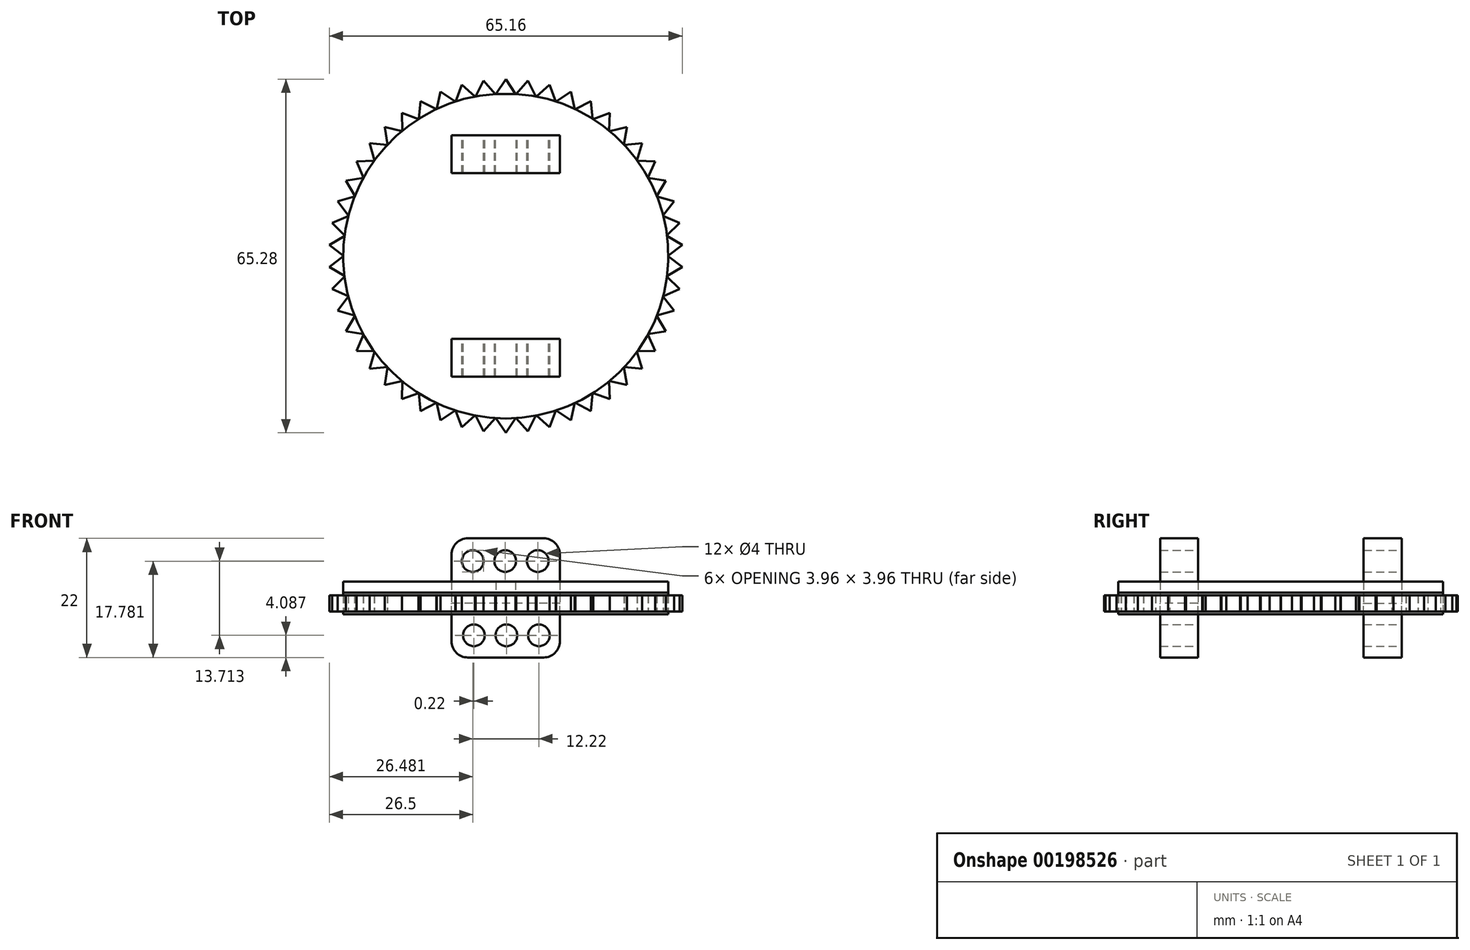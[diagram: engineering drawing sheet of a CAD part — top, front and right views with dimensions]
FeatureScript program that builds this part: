
annotation { "Feature Type Name" : "Feature", "Feature Type Description" : "" }
export const myFeature = defineFeature(function(context is Context, id is Id, definition is map)
    precondition{}
    {
        {
            var Q0;
            Q0=qCreatedBy(makeId("Top.planeOp"),FACE);
            var sketch = newSketch(context, id + "F0", { "sketchPlane" : qUnion([Q0])});
            skCircle(sketch, "E0", {"center": v(0, 0) * mm, "radius": 30 * mm});
            skLineSegment(sketch, "E1", {"start": v(0, 35.87) * mm, "end": v(0, -34.78) * mm, "construction": true});
            skLineSegment(sketch, "E2", {"start": v(-1.83, 29.94) * mm, "end": v(0, 32.64) * mm});
            skLineSegment(sketch, "E3.MirrorCS", {"start": v(1.83, 29.94) * mm, "end": v(0, 32.64) * mm});
            skLineSegment(sketch, "E4", {"start": v(-1.83, 29.94) * mm, "end": v(1.83, 29.94) * mm});
            skLineSegment(sketch, "E5.1.0", {"start": v(-5.57, 29.48) * mm, "end": v(-4.1, 32.39) * mm});
            skLineSegment(sketch, "E5.1.1", {"start": v(-1.94, 29.94) * mm, "end": v(-4.1, 32.39) * mm});
            skLineSegment(sketch, "E5.2.0", {"start": v(-9.22, 28.55) * mm, "end": v(-8.12, 31.62) * mm});
            skLineSegment(sketch, "E5.2.1", {"start": v(-5.68, 29.46) * mm, "end": v(-8.12, 31.62) * mm});
            skLineSegment(sketch, "E5.3.0", {"start": v(-12.72, 27.17) * mm, "end": v(-12.02, 30.35) * mm});
            skLineSegment(sketch, "E5.3.1", {"start": v(-9.33, 28.51) * mm, "end": v(-12.02, 30.35) * mm});
            skLineSegment(sketch, "E5.4.0", {"start": v(-16.03, 25.36) * mm, "end": v(-15.73, 28.6) * mm});
            skLineSegment(sketch, "E5.4.1", {"start": v(-12.83, 27.12) * mm, "end": v(-15.73, 28.6) * mm});
            skLineSegment(sketch, "E5.5.0", {"start": v(-19.08, 23.15) * mm, "end": v(-19.19, 26.4) * mm});
            skLineSegment(sketch, "E5.5.1", {"start": v(-16.12, 25.3) * mm, "end": v(-19.19, 26.4) * mm});
            skLineSegment(sketch, "E5.6.0", {"start": v(-21.83, 20.58) * mm, "end": v(-22.35, 23.8) * mm});
            skLineSegment(sketch, "E5.6.1", {"start": v(-19.17, 23.08) * mm, "end": v(-22.35, 23.8) * mm});
            skLineSegment(sketch, "E5.7.0", {"start": v(-24.24, 17.68) * mm, "end": v(-25.15, 20.8) * mm});
            skLineSegment(sketch, "E5.7.1", {"start": v(-21.9, 20.5) * mm, "end": v(-25.15, 20.8) * mm});
            skLineSegment(sketch, "E5.8.0", {"start": v(-26.26, 14.5) * mm, "end": v(-27.56, 17.5) * mm});
            skLineSegment(sketch, "E5.8.1", {"start": v(-24.3, 17.59) * mm, "end": v(-27.56, 17.5) * mm});
            skLineSegment(sketch, "E5.9.0", {"start": v(-27.87, 11.1) * mm, "end": v(-29.54, 13.9) * mm});
            skLineSegment(sketch, "E5.9.1", {"start": v(-26.32, 14.4) * mm, "end": v(-29.54, 13.9) * mm});
            skLineSegment(sketch, "E5.10.0", {"start": v(-29.04, 7.52) * mm, "end": v(-31.05, 10.09) * mm});
            skLineSegment(sketch, "E5.10.1", {"start": v(-27.91, 11) * mm, "end": v(-31.05, 10.09) * mm});
            skLineSegment(sketch, "E5.11.0", {"start": v(-29.76, 3.82) * mm, "end": v(-32.07, 6.12) * mm});
            skLineSegment(sketch, "E5.11.1", {"start": v(-29.07, 7.4) * mm, "end": v(-32.07, 6.12) * mm});
            skLineSegment(sketch, "E5.12.0", {"start": v(-30, 0.06) * mm, "end": v(-32.58, 2.05) * mm});
            skLineSegment(sketch, "E5.12.1", {"start": v(-29.77, 3.7) * mm, "end": v(-32.58, 2.05) * mm});
            skLineSegment(sketch, "E5.13.0", {"start": v(-29.77, -3.7) * mm, "end": v(-32.58, -2.05) * mm});
            skLineSegment(sketch, "E5.13.1", {"start": v(-30, -0.06) * mm, "end": v(-32.58, -2.05) * mm});
            skLineSegment(sketch, "E5.14.0", {"start": v(-29.07, -7.4) * mm, "end": v(-32.07, -6.12) * mm});
            skLineSegment(sketch, "E5.14.1", {"start": v(-29.76, -3.82) * mm, "end": v(-32.07, -6.12) * mm});
            skLineSegment(sketch, "E5.15.0", {"start": v(-27.91, -11) * mm, "end": v(-31.05, -10.09) * mm});
            skLineSegment(sketch, "E5.15.1", {"start": v(-29.04, -7.52) * mm, "end": v(-31.05, -10.09) * mm});
            skLineSegment(sketch, "E5.16.0", {"start": v(-26.32, -14.4) * mm, "end": v(-29.54, -13.9) * mm});
            skLineSegment(sketch, "E5.16.1", {"start": v(-27.87, -11.1) * mm, "end": v(-29.54, -13.9) * mm});
            skLineSegment(sketch, "E5.17.0", {"start": v(-24.3, -17.59) * mm, "end": v(-27.56, -17.5) * mm});
            skLineSegment(sketch, "E5.17.1", {"start": v(-26.26, -14.5) * mm, "end": v(-27.56, -17.5) * mm});
            skLineSegment(sketch, "E5.18.0", {"start": v(-21.9, -20.5) * mm, "end": v(-25.15, -20.8) * mm});
            skLineSegment(sketch, "E5.18.1", {"start": v(-24.24, -17.68) * mm, "end": v(-25.15, -20.8) * mm});
            skLineSegment(sketch, "E5.19.0", {"start": v(-19.17, -23.08) * mm, "end": v(-22.35, -23.8) * mm});
            skLineSegment(sketch, "E5.19.1", {"start": v(-21.83, -20.58) * mm, "end": v(-22.35, -23.8) * mm});
            skLineSegment(sketch, "E5.20.0", {"start": v(-16.12, -25.3) * mm, "end": v(-19.19, -26.4) * mm});
            skLineSegment(sketch, "E5.20.1", {"start": v(-19.08, -23.15) * mm, "end": v(-19.19, -26.4) * mm});
            skLineSegment(sketch, "E5.21.0", {"start": v(-12.83, -27.12) * mm, "end": v(-15.73, -28.6) * mm});
            skLineSegment(sketch, "E5.21.1", {"start": v(-16.03, -25.36) * mm, "end": v(-15.73, -28.6) * mm});
            skLineSegment(sketch, "E5.22.0", {"start": v(-9.33, -28.51) * mm, "end": v(-12.02, -30.35) * mm});
            skLineSegment(sketch, "E5.22.1", {"start": v(-12.72, -27.17) * mm, "end": v(-12.02, -30.35) * mm});
            skLineSegment(sketch, "E5.23.0", {"start": v(-5.68, -29.46) * mm, "end": v(-8.12, -31.62) * mm});
            skLineSegment(sketch, "E5.23.1", {"start": v(-9.22, -28.55) * mm, "end": v(-8.12, -31.62) * mm});
            skLineSegment(sketch, "E5.24.0", {"start": v(-1.94, -29.94) * mm, "end": v(-4.1, -32.39) * mm});
            skLineSegment(sketch, "E5.24.1", {"start": v(-5.57, -29.48) * mm, "end": v(-4.1, -32.39) * mm});
            skLineSegment(sketch, "E5.25.0", {"start": v(1.83, -29.94) * mm, "end": v(0, -32.64) * mm});
            skLineSegment(sketch, "E5.25.1", {"start": v(-1.83, -29.94) * mm, "end": v(0, -32.64) * mm});
            skLineSegment(sketch, "E5.26.0", {"start": v(5.57, -29.48) * mm, "end": v(4.1, -32.39) * mm});
            skLineSegment(sketch, "E5.26.1", {"start": v(1.94, -29.94) * mm, "end": v(4.1, -32.39) * mm});
            skLineSegment(sketch, "E5.27.0", {"start": v(9.22, -28.55) * mm, "end": v(8.12, -31.62) * mm});
            skLineSegment(sketch, "E5.27.1", {"start": v(5.68, -29.46) * mm, "end": v(8.12, -31.62) * mm});
            skLineSegment(sketch, "E5.28.0", {"start": v(12.72, -27.17) * mm, "end": v(12.02, -30.35) * mm});
            skLineSegment(sketch, "E5.28.1", {"start": v(9.33, -28.51) * mm, "end": v(12.02, -30.35) * mm});
            skLineSegment(sketch, "E5.29.0", {"start": v(16.03, -25.36) * mm, "end": v(15.73, -28.6) * mm});
            skLineSegment(sketch, "E5.29.1", {"start": v(12.83, -27.12) * mm, "end": v(15.73, -28.6) * mm});
            skLineSegment(sketch, "E5.30.0", {"start": v(19.08, -23.15) * mm, "end": v(19.19, -26.4) * mm});
            skLineSegment(sketch, "E5.30.1", {"start": v(16.12, -25.3) * mm, "end": v(19.19, -26.4) * mm});
            skLineSegment(sketch, "E5.31.0", {"start": v(21.83, -20.58) * mm, "end": v(22.35, -23.8) * mm});
            skLineSegment(sketch, "E5.31.1", {"start": v(19.17, -23.08) * mm, "end": v(22.35, -23.8) * mm});
            skLineSegment(sketch, "E5.32.0", {"start": v(24.24, -17.68) * mm, "end": v(25.15, -20.8) * mm});
            skLineSegment(sketch, "E5.32.1", {"start": v(21.9, -20.5) * mm, "end": v(25.15, -20.8) * mm});
            skLineSegment(sketch, "E5.33.0", {"start": v(26.26, -14.5) * mm, "end": v(27.56, -17.5) * mm});
            skLineSegment(sketch, "E5.33.1", {"start": v(24.3, -17.59) * mm, "end": v(27.56, -17.5) * mm});
            skLineSegment(sketch, "E5.34.0", {"start": v(27.87, -11.1) * mm, "end": v(29.54, -13.9) * mm});
            skLineSegment(sketch, "E5.34.1", {"start": v(26.32, -14.4) * mm, "end": v(29.54, -13.9) * mm});
            skLineSegment(sketch, "E5.35.0", {"start": v(29.04, -7.52) * mm, "end": v(31.05, -10.09) * mm});
            skLineSegment(sketch, "E5.35.1", {"start": v(27.91, -11) * mm, "end": v(31.05, -10.09) * mm});
            skLineSegment(sketch, "E5.36.0", {"start": v(29.76, -3.82) * mm, "end": v(32.07, -6.12) * mm});
            skLineSegment(sketch, "E5.36.1", {"start": v(29.07, -7.4) * mm, "end": v(32.07, -6.12) * mm});
            skLineSegment(sketch, "E5.37.0", {"start": v(30, -0.06) * mm, "end": v(32.58, -2.05) * mm});
            skLineSegment(sketch, "E5.37.1", {"start": v(29.77, -3.7) * mm, "end": v(32.58, -2.05) * mm});
            skLineSegment(sketch, "E5.38.0", {"start": v(29.77, 3.7) * mm, "end": v(32.58, 2.05) * mm});
            skLineSegment(sketch, "E5.38.1", {"start": v(30, 0.06) * mm, "end": v(32.58, 2.05) * mm});
            skLineSegment(sketch, "E5.39.0", {"start": v(29.07, 7.4) * mm, "end": v(32.07, 6.12) * mm});
            skLineSegment(sketch, "E5.39.1", {"start": v(29.76, 3.82) * mm, "end": v(32.07, 6.12) * mm});
            skLineSegment(sketch, "E5.40.0", {"start": v(27.91, 11) * mm, "end": v(31.05, 10.09) * mm});
            skLineSegment(sketch, "E5.40.1", {"start": v(29.04, 7.52) * mm, "end": v(31.05, 10.09) * mm});
            skLineSegment(sketch, "E5.41.0", {"start": v(26.32, 14.4) * mm, "end": v(29.54, 13.9) * mm});
            skLineSegment(sketch, "E5.41.1", {"start": v(27.87, 11.1) * mm, "end": v(29.54, 13.9) * mm});
            skLineSegment(sketch, "E5.42.0", {"start": v(24.3, 17.59) * mm, "end": v(27.56, 17.5) * mm});
            skLineSegment(sketch, "E5.42.1", {"start": v(26.26, 14.5) * mm, "end": v(27.56, 17.5) * mm});
            skLineSegment(sketch, "E5.43.0", {"start": v(21.9, 20.5) * mm, "end": v(25.15, 20.8) * mm});
            skLineSegment(sketch, "E5.43.1", {"start": v(24.24, 17.68) * mm, "end": v(25.15, 20.8) * mm});
            skLineSegment(sketch, "E5.44.0", {"start": v(19.17, 23.08) * mm, "end": v(22.35, 23.8) * mm});
            skLineSegment(sketch, "E5.44.1", {"start": v(21.83, 20.58) * mm, "end": v(22.35, 23.8) * mm});
            skLineSegment(sketch, "E5.45.0", {"start": v(16.12, 25.3) * mm, "end": v(19.19, 26.4) * mm});
            skLineSegment(sketch, "E5.45.1", {"start": v(19.08, 23.15) * mm, "end": v(19.19, 26.4) * mm});
            skLineSegment(sketch, "E5.46.0", {"start": v(12.83, 27.12) * mm, "end": v(15.73, 28.6) * mm});
            skLineSegment(sketch, "E5.46.1", {"start": v(16.03, 25.36) * mm, "end": v(15.73, 28.6) * mm});
            skLineSegment(sketch, "E5.47.0", {"start": v(9.33, 28.51) * mm, "end": v(12.02, 30.35) * mm});
            skLineSegment(sketch, "E5.47.1", {"start": v(12.72, 27.17) * mm, "end": v(12.02, 30.35) * mm});
            skLineSegment(sketch, "E5.48.0", {"start": v(5.68, 29.46) * mm, "end": v(8.12, 31.62) * mm});
            skLineSegment(sketch, "E5.48.1", {"start": v(9.22, 28.55) * mm, "end": v(8.12, 31.62) * mm});
            skLineSegment(sketch, "E5.49.0", {"start": v(1.94, 29.94) * mm, "end": v(4.1, 32.39) * mm});
            skLineSegment(sketch, "E5.49.1", {"start": v(5.57, 29.48) * mm, "end": v(4.1, 32.39) * mm});
            skSolve(sketch);
        }
        {
            var Q0;
            Q0 = qSketchRegion(id + "F0", true);
            extrude(context, id + "F1", {"entities" : qUnion([Q0]), "endBound" : BoundingType.SYMMETRIC, "depth" : 3 * mm});
        }
        {
            var Q0;
            {var subQ56=sQuery(id+"F0.wireOp",EDGE,"E4");Q0=makeQuery(id+"F0.imprint","IMPRINT",FACE,{"disambiguationData":[TD([[makeQuery(id+"F0.imprint","IMPRINT",EDGE,{"derivedFrom":subQ56}),-1.0]])]});}
            extrude(context, id + "F2", {"entities" : qUnion([Q0]), "endBound" : BoundingType.SYMMETRIC, "depth" : 4 * mm});
        }
        {
            var Q0;
            Q0=makeQuery(id+"F2.opExtrude","CAP_FACE",FACE,{"disambiguationData":[OSD([sQuery(id+"F0.wireOp",EDGE,"E0"),sQuery(id+"F0.wireOp",EDGE,"E4")])],"isStart":false});
            var Q1;
            Q1=sQuery(id+"F0.wireOp",EDGE,"E0");
            extrude(context, id + "F3", {"entities" : qUnion([Q0]), "surfaceEntities" : qUnion([Q1]), "depth" : 2 * mm});
        }
        {
            var Q0;
            Q0=qCreatedBy(makeId("Top.planeOp"),FACE);
            var sketch = newSketch(context, id + "F4", { "sketchPlane" : qUnion([Q0])});
            skLineSegment(sketch, "E6.bottom", {"start": v(10, 15.28) * mm, "end": v(-10, 15.28) * mm});
            skLineSegment(sketch, "E6.top", {"start": v(10, 22.28) * mm, "end": v(-10, 22.28) * mm});
            skLineSegment(sketch, "E6.left", {"start": v(10, 15.28) * mm, "end": v(10, 22.28) * mm});
            skLineSegment(sketch, "E6.right", {"start": v(-10, 15.28) * mm, "end": v(-10, 22.28) * mm});
            skLineSegment(sketch, "E7", {"start": v(0, -38.44) * mm, "end": v(0, 57.13) * mm, "construction": true});
            skLineSegment(sketch, "E8", {"start": v(36.72, 0) * mm, "end": v(-39.04, 0) * mm, "construction": true});
            skSolve(sketch);
        }
        {
            var Q0;
            Q0 = qSketchRegion(id + "F4", true);
            extrude(context, id + "F5", {"entities" : qUnion([Q0]), "depth" : 12 * mm});
        }
        {
            var Q0;
            Q0=makeQuery(id+"F5.opExtrude","CAP_EDGE",EDGE,{"disambiguationData":[OSD([sQuery(id+"F4.wireOp",EDGE,"E6.left")])],"isStart":false});
            var Q1;
            Q1=makeQuery(id+"F5.opExtrude","CAP_EDGE",EDGE,{"disambiguationData":[OSD([sQuery(id+"F4.wireOp",EDGE,"E6.right")])],"isStart":false});
            fillet(context, id + "F6", {"entities" : qUnion([Q0, Q1]), "radius" : 3 * mm, "tangentPropagation" : true, "allowEdgeOverflow" : false});
        }
        {
            var Q0;
            Q0=makeQuery(id+"F5.opExtrude","SWEPT_BODY",BODY,{"disambiguationData":[OSD([sQuery(id+"F4.wireOp",EDGE,"E6.bottom"),sQuery(id+"F4.wireOp",EDGE,"E6.top"),sQuery(id+"F4.wireOp",EDGE,"E6.left"),sQuery(id+"F4.wireOp",EDGE,"E6.right")])]});
            var Q1;
            Q1=qCreatedBy(makeId("Front.planeOp"),FACE);
            mirror(context, id + "F7", {"entities" : qUnion([Q0]), "mirrorPlane" : qUnion([Q1])});
        }
        {
            var Q0;
            Q0=qCreatedBy(makeId("Front.planeOp"),FACE);
            var sketch = newSketch(context, id + "F8", { "sketchPlane" : qUnion([Q0])});
            skCircle(sketch, "E9", {"center": v(5.9, 7.8) * mm, "radius": 2 * mm});
            skCircle(sketch, "E10.1.0.0", {"center": v(-0.1, 7.8) * mm, "radius": 2 * mm});
            skCircle(sketch, "E10.2.0.0", {"center": v(-6.1, 7.8) * mm, "radius": 2 * mm});
            skLineSegment(sketch, "E10.direction1", {"start": v(5.9, 7.8) * mm, "end": v(-0.1, 7.8) * mm, "construction": true});
            skSolve(sketch);
        }
        {
            var Q0;
            Q0 = qSketchRegion(id + "F8", true);
            extrude(context, id + "F9", {"entities" : qUnion([Q0]), "operationType" : NewBodyOperationType.REMOVE, "endBound" : BoundingType.SYMMETRIC, "depth" : 50 * mm});
        }
        {
            var Q0;
            Q0 = qSketchRegion(id + "F4", true);
            extrude(context, id + "F10", {"entities" : qUnion([Q0]), "oppositeDirection" : true, "depth" : 10 * mm});
        }
        {
            var Q0;
            Q0=makeQuery(id+"F10.opExtrude","CAP_EDGE",EDGE,{"disambiguationData":[OSD([sQuery(id+"F4.wireOp",EDGE,"E6.left")])],"isStart":false});
            var Q1;
            Q1=makeQuery(id+"F10.opExtrude","CAP_EDGE",EDGE,{"disambiguationData":[OSD([sQuery(id+"F4.wireOp",EDGE,"E6.right")])],"isStart":false});
            fillet(context, id + "F11", {"entities" : qUnion([Q0, Q1]), "radius" : 3 * mm, "tangentPropagation" : true, "allowEdgeOverflow" : false});
        }
        {
            var Q0;
            Q0=makeQuery(id+"F10.opExtrude","SWEPT_BODY",BODY,{"disambiguationData":[OSD([sQuery(id+"F4.wireOp",EDGE,"E6.bottom"),sQuery(id+"F4.wireOp",EDGE,"E6.top"),sQuery(id+"F4.wireOp",EDGE,"E6.left"),sQuery(id+"F4.wireOp",EDGE,"E6.right")])]});
            var Q1;
            Q1=qCreatedBy(makeId("Front.planeOp"),FACE);
            mirror(context, id + "F12", {"entities" : qUnion([Q0]), "mirrorPlane" : qUnion([Q1])});
        }
        {
            var Q0;
            Q0=qCreatedBy(makeId("Front.planeOp"),FACE);
            var sketch = newSketch(context, id + "F13", { "sketchPlane" : qUnion([Q0])});
            skCircle(sketch, "E11", {"center": v(6.12, -5.91) * mm, "radius": 2 * mm});
            skCircle(sketch, "E12.1.0.0", {"center": v(0.12, -5.91) * mm, "radius": 2 * mm});
            skCircle(sketch, "E12.2.0.0", {"center": v(-5.88, -5.91) * mm, "radius": 2 * mm});
            skLineSegment(sketch, "E12.direction1", {"start": v(6.12, -5.91) * mm, "end": v(0.12, -5.91) * mm, "construction": true});
            skSolve(sketch);
        }
        {
            var Q0;
            Q0 = qSketchRegion(id + "F13", true);
            var Q1;
            Q1=sQuery(id+"F13.wireOp",EDGE,"E11");
            var Q2;
            Q2=sQuery(id+"F13.wireOp",EDGE,"E12.1.0.0");
            var Q3;
            Q3=sQuery(id+"F13.wireOp",EDGE,"E12.2.0.0");
            extrude(context, id + "F14", {"entities" : qUnion([Q0]), "operationType" : NewBodyOperationType.REMOVE, "surfaceEntities" : qUnion([Q1, Q2, Q3]), "endBound" : BoundingType.SYMMETRIC, "depth" : 50 * mm});
        }
    });
